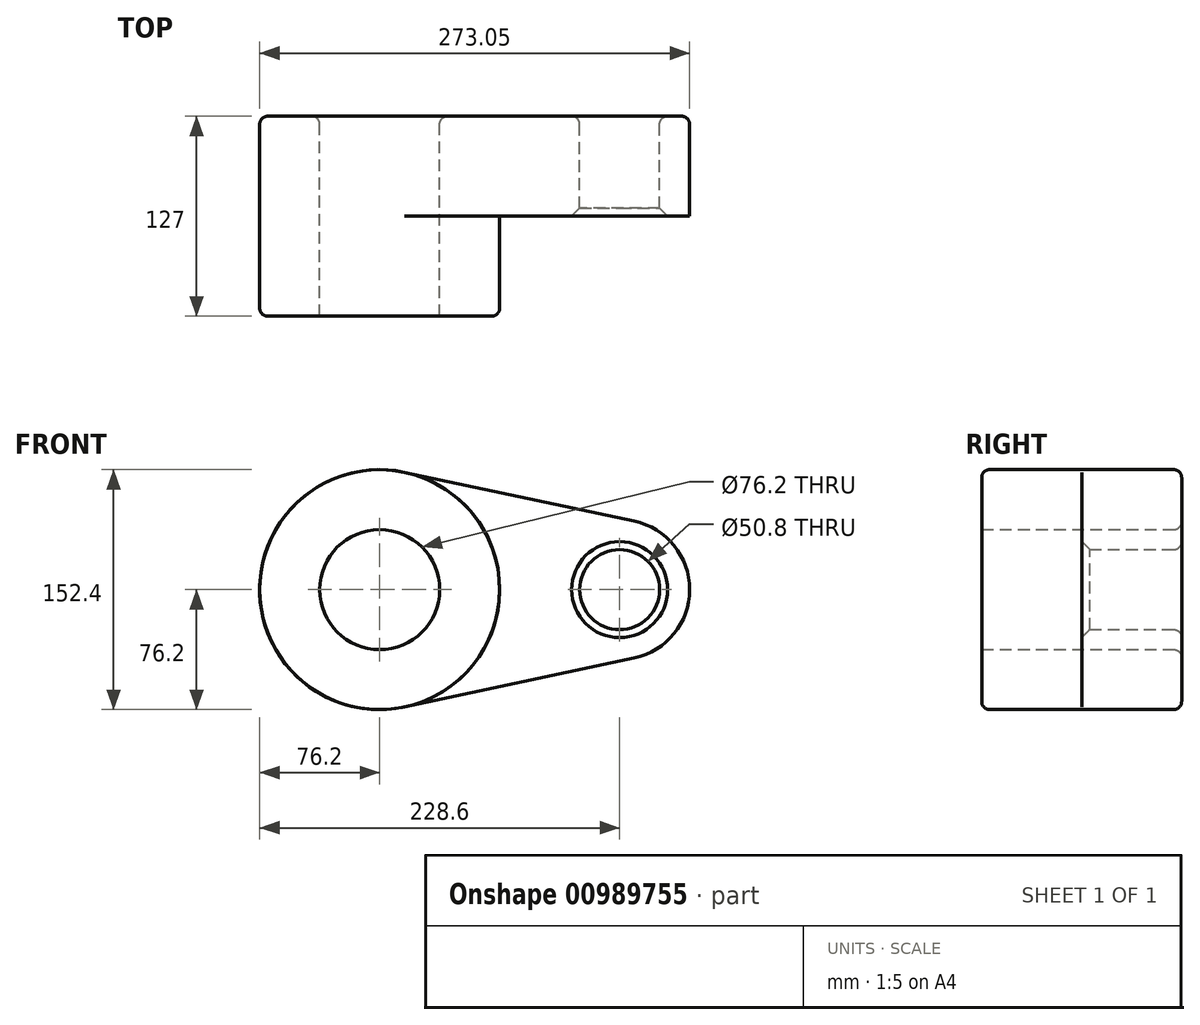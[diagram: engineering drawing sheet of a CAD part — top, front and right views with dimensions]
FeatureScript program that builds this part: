
annotation { "Feature Type Name" : "Feature", "Feature Type Description" : "" }
export const myFeature = defineFeature(function(context is Context, id is Id, definition is map)
    precondition{}
    {
        {
            var Q0;
            Q0=qCreatedBy(makeId("Front.planeOp"),FACE);
            var sketch = newSketch(context, id + "F0", { "sketchPlane" : qUnion([Q0])});
            skCircle(sketch, "E0", {"center": v(0, 0) * mm, "radius": 76.2 * mm});
            skCircle(sketch, "E1", {"center": v(152.4, 0) * mm, "radius": 44.45 * mm});
            skLineSegment(sketch, "E2", {"start": v(15.87, 74.53) * mm, "end": v(161.66, 43.47) * mm});
            skLineSegment(sketch, "E3", {"start": v(15.87, -74.53) * mm, "end": v(161.66, -43.47) * mm});
            skCircle(sketch, "E4", {"center": v(0, 0) * mm, "radius": 38.1 * mm});
            skCircle(sketch, "E5", {"center": v(152.4, 0) * mm, "radius": 25.4 * mm});
            skSolve(sketch);
        }
        {
            var Q0;
            Q0 = qSketchRegion(id + "F0", true);
            extrude(context, id + "F1", {"entities" : qUnion([Q0]), "depth" : 63.5 * mm, "offsetDistance" : 25.4 * mm});
        }
        {
            var Q0;
            Q0=makeQuery(id+"F0.imprint","IMPRINT",FACE,{"disambiguationData":[TD([[makeQuery(id+"F0.imprint","IMPRINT",EDGE,{"derivedFrom":sQuery(id+"F0.wireOp",EDGE,"E4")}),-1.0]])]});
            extrude(context, id + "F2", {"entities" : qUnion([Q0]), "operationType" : NewBodyOperationType.ADD, "depth" : 127 * mm, "offsetDistance" : 25.4 * mm});
        }
        {
            var Q0;
            Q0=makeQuery(id+"F2.opExtrude","CAP_EDGE",EDGE,{"disambiguationData":[OSD([sQuery(id+"F0.wireOp",EDGE,"E0")])],"isStart":false});
            var Q1;
            Q1=makeQuery(id+"F1.opExtrude","CAP_FACE",FACE,{"disambiguationData":[OSD([sQuery(id+"F0.wireOp",EDGE,"E0"),sQuery(id+"F0.wireOp",EDGE,"E1"),sQuery(id+"F0.wireOp",EDGE,"E2"),sQuery(id+"F0.wireOp",EDGE,"E3"),sQuery(id+"F0.wireOp",EDGE,"E4"),sQuery(id+"F0.wireOp",EDGE,"E5")])],"isStart":true});
            fillet(context, id + "F3", {"entities" : qUnion([Q0, Q1]), "radius" : 5.08 * mm, "tangentPropagation" : true, "allowEdgeOverflow" : false});
        }
        {
            var Q0;
            Q0=makeQuery(id+"F1.opExtrude","CAP_EDGE",EDGE,{"disambiguationData":[OSD([sQuery(id+"F0.wireOp",EDGE,"E5")])],"isStart":false});
            chamfer(context, id + "F4", {"entities" : qUnion([Q0]), "width" : 5.08 * mm, "tangentPropagation" : true});
        }
    });
